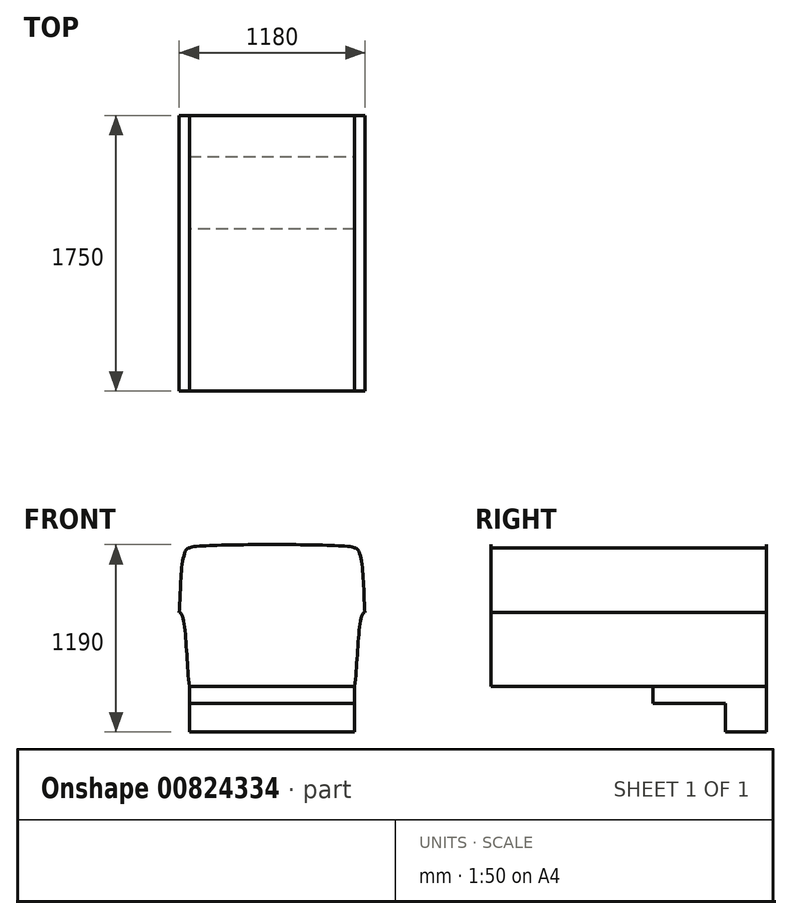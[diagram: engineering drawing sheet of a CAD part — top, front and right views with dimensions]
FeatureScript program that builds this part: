
annotation { "Feature Type Name" : "Feature", "Feature Type Description" : "" }
export const myFeature = defineFeature(function(context is Context, id is Id, definition is map)
    precondition{}
    {
        {
            var Q0;
            Q0=qCreatedBy(makeId("Front.planeOp"),FACE);
            var sketch = newSketch(context, id + "F0", { "sketchPlane" : qUnion([Q0])});
            skLineSegment(sketch, "E0", {"start": v(5.62, -442.72) * mm, "end": v(530.62, -442.72) * mm});
            skLineSegment(sketch, "E1", {"start": v(5.62, -442.72) * mm, "end": v(-519.38, -442.72) * mm});
            skFitSpline(sketch, "E2", {"points": [v(-519.38, -442.72) * mm, v(-584.38, 27.28) * mm], "startDerivative": vector(-65, 470) * mm, "endDerivative": vector(-143.92, 0) * mm});
            skFitSpline(sketch, "E3.MirrorCS", {"points": [v(530.62, -442.72) * mm, v(595.62, 27.28) * mm], "startDerivative": vector(65, 470) * mm, "endDerivative": vector(143.92, 0) * mm});
            skFitSpline(sketch, "E4", {"points": [v(-584.38, 27.28) * mm, v(-519.38, 437.28) * mm], "startDerivative": vector(33.21, 380.54) * mm, "endDerivative": vector(183.93, 8.08) * mm});
            skFitSpline(sketch, "E5.MirrorCS", {"points": [v(595.62, 27.28) * mm, v(530.62, 437.28) * mm], "startDerivative": vector(-33.21, 380.54) * mm, "endDerivative": vector(-183.93, 8.08) * mm});
            skFitSpline(sketch, "E6", {"points": [v(-519.38, 437.28) * mm, v(5.62, 457.28) * mm], "startDerivative": vector(137.12, 58.34) * mm, "endDerivative": vector(502.4, 1.66) * mm});
            skFitSpline(sketch, "E7.MirrorCS", {"points": [v(530.62, 437.28) * mm, v(5.62, 457.28) * mm], "startDerivative": vector(-137.12, 58.34) * mm, "endDerivative": vector(-502.4, 1.66) * mm});
            skLineSegment(sketch, "E8", {"start": v(-519.38, -442.72) * mm, "end": v(-519.38, -552.72) * mm});
            skLineSegment(sketch, "E9", {"start": v(-519.38, -552.72) * mm, "end": v(530.62, -552.72) * mm});
            skLineSegment(sketch, "E10", {"start": v(530.62, -552.72) * mm, "end": v(530.62, -442.72) * mm});
            skLineSegment(sketch, "E11", {"start": v(-519.38, -552.72) * mm, "end": v(-519.38, -732.72) * mm});
            skLineSegment(sketch, "E12", {"start": v(-519.38, -732.72) * mm, "end": v(530.62, -732.72) * mm});
            skLineSegment(sketch, "E13", {"start": v(530.62, -732.72) * mm, "end": v(530.62, -552.72) * mm});
            skSolve(sketch);
        }
        {
            var Q0;
            Q0=makeQuery(id+"F0.imprint","IMPRINT",FACE,{"disambiguationData":[TD([[makeQuery(id+"F0.imprint","IMPRINT",EDGE,{"derivedFrom":sQuery(id+"F0.wireOp",EDGE,"E0")}),1.0]])]});
            extrude(context, id + "F1", {"entities" : qUnion([Q0]), "oppositeDirection" : true, "depth" : 260 * mm, "offsetDistance" : 25 * mm});
        }
        {
            var Q0;
            Q0=makeQuery(id+"F0.imprint","IMPRINT",FACE,{"disambiguationData":[TD([[makeQuery(id+"F0.imprint","IMPRINT",EDGE,{"derivedFrom":sQuery(id+"F0.wireOp",EDGE,"E0")}),-1.0]])]});
            extrude(context, id + "F2", {"entities" : qUnion([Q0]), "operationType" : NewBodyOperationType.ADD, "oppositeDirection" : true, "depth" : 260 * mm, "offsetDistance" : 25 * mm});
        }
        {
            var Q0;
            Q0=makeQuery(id+"F0.imprint","IMPRINT",FACE,{"disambiguationData":[TD([[makeQuery(id+"F0.imprint","IMPRINT",EDGE,{"derivedFrom":sQuery(id+"F0.wireOp",EDGE,"E9")}),-1.0]])]});
            extrude(context, id + "F3", {"entities" : qUnion([Q0]), "operationType" : NewBodyOperationType.ADD, "oppositeDirection" : true, "depth" : 260 * mm, "offsetDistance" : 25 * mm});
        }
        {
            var Q0;
            Q0=makeQuery(id+"F0.imprint","IMPRINT",FACE,{"disambiguationData":[TD([[makeQuery(id+"F0.imprint","IMPRINT",EDGE,{"derivedFrom":sQuery(id+"F0.wireOp",EDGE,"E0")}),1.0]])]});
            extrude(context, id + "F4", {"entities" : qUnion([Q0]), "operationType" : NewBodyOperationType.ADD, "depth" : 1490 * mm, "offsetDistance" : 25 * mm});
        }
        {
            var Q0;
            Q0=makeQuery(id+"F0.imprint","IMPRINT",FACE,{"disambiguationData":[TD([[makeQuery(id+"F0.imprint","IMPRINT",EDGE,{"derivedFrom":sQuery(id+"F0.wireOp",EDGE,"E0")}),-1.0]])]});
            extrude(context, id + "F5", {"entities" : qUnion([Q0]), "operationType" : NewBodyOperationType.ADD, "depth" : 460 * mm, "offsetDistance" : 25 * mm});
        }
    });
